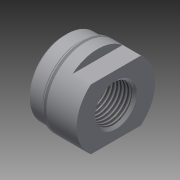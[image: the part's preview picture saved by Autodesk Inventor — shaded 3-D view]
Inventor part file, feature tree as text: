
AUTODESK INVENTOR PART (.ipt)
format: ipt  version: 2014 SP2 (Build 180246200, 246)  size: 219,648 bytes
history: native  units: in
note: dims shown in document units (in); Inventor stores cm internally (conversion verified against a paired STEP export)
features: other x112, sketch x4, revolve x3, thread x1, extrude x1
ambient origin geometry x8: Origin, YZ Plane, XZ Plane, XY Plane, X Axis, Y Axis, Z Axis, Center Point
bodies: Solid1 (feature_tree)
feature tree (121):
  revolve  "Revolution1"  Angle=360.0deg
  revolve  "Revolution2"  [1 undecoded]
  thread  "Thread1"  [1 undecoded]
  extrude  "Extrusion1"  [1 undecoded]
  revolve  "Revolution3"  [1 undecoded]
  other  "cut1_XY"
  other  "cut1_YZ"
  other  "cut1_ZX"
  other  "cut1_X"
  other  "cut1_Y"
  other  "cut1_Z"
  other  "cut1_Center"
  other  "cut2_XY"
  other  "cut2_YZ"
  other  "cut2_ZX"
  other  "cut2_X"
  other  "cut2_Y"
  other  "cut2_Z"
  other  "cut2_Center"
  other  "cutf1_XY"
  other  "cutf1_YZ"
  other  "cutf1_ZX"
  other  "cutf1_X"
  other  "cutf1_Y"
  other  "cutf1_Z"
  other  "cutf1_Center"
  other  "cutf2_XY"
  other  "cutf2_YZ"
  other  "cutf2_ZX"
  other  "cutf2_X"
  other  "cutf2_Y"
  other  "cutf2_Z"
  other  "cutf2_Center"
  other  "lovra_XY"
  other  "lovra_YZ"
  other  "lovra_ZX"
  other  "lovra_X"
  other  "lovra_Y"
  other  "lovra_Z"
  other  "lovra_Center"
  other  "lovra1_XY"
  other  "lovra1_YZ"
  other  "lovra1_ZX"
  other  "lovra1_X"
  other  "lovra1_Y"
  other  "lovra1_Z"
  other  "lovra1_Center"
  other  "lovra2_XY"
  other  "lovra2_YZ"
  other  "lovra2_ZX"
  other  "lovra2_X"
  other  "lovra2_Y"
  other  "lovra2_Z"
  other  "lovra2_Center"
  other  "lovra21_XY"
  other  "lovra21_YZ"
  other  "lovra21_ZX"
  other  "lovra21_X"
  other  "lovra21_Y"
  other  "lovra21_Z"
  other  "lovra21_Center"
  other  "lovra22_XY"
  other  "lovra22_YZ"
  other  "lovra22_ZX"
  other  "lovra22_X"
  other  "lovra22_Y"
  other  "lovra22_Z"
  other  "lovra22_Center"
  other  "lovra3_XY"
  other  "lovra3_YZ"
  other  "lovra3_ZX"
  other  "lovra3_X"
  other  "lovra3_Y"
  other  "lovra3_Z"
  other  "lovra3_Center"
  other  "olen_XY"
  other  "olen_YZ"
  other  "olen_ZX"
  other  "olen_X"
  other  "olen_Y"
  other  "olen_Z"
  other  "olen_Center"
  other  "to_mounting_bracket_XY"
  other  "to_mounting_bracket_YZ"
  other  "to_mounting_bracket_ZX"
  other  "to_mounting_bracket_X"
  other  "to_mounting_bracket_Y"
  other  "to_mounting_bracket_Z"
  other  "to_mounting_bracket_Center"
  other  "to_nut_XY"
  other  "to_nut_YZ"
  other  "to_nut_ZX"
  other  "to_nut_X"
  other  "to_nut_Y"
  other  "to_nut_Z"
  other  "to_nut_Center"
  other  "to_pin_XY"
  other  "to_pin_YZ"
  other  "to_pin_ZX"
  other  "to_pin_X"
  other  "to_pin_Y"
  other  "to_pin_Z"
  other  "to_pin_Center"
  other  "to_screw_XY"
  other  "to_screw_YZ"
  other  "to_screw_ZX"
  other  "to_screw_X"
  other  "to_screw_Y"
  other  "to_screw_Z"
  other  "to_screw_Center"
  other  "to_tube_XY"
  other  "to_tube_YZ"
  other  "to_tube_ZX"
  other  "to_tube_X"
  other  "to_tube_Y"
  other  "to_tube_Z"
  other  "to_tube_Center"
  sketch  "Sketch_1"  dims[d0=360.0deg d1=360.0deg]
  sketch  "Sketch_6"  dims[d7=0.0in d8=0.0in d9=0.0in d10=0.0in d11=0.0in d12=0.0in d13=0.0in d14=0.0in d15=0.0in d16=0.0in]
  sketch  "Sketch_5"  dims[d2=0.2771in d3=0.0in d4=0.188in d5=0.0in d6=360.0deg]
  sketch  "Sketch_24"
note: 4 required parameter values undecoded (feature->parameter linkage not recoverable at this tier; creation-order binding heuristic only, values carry confidence <= 0.55)